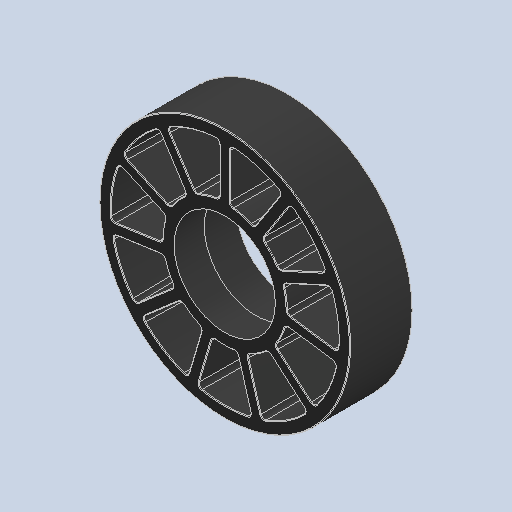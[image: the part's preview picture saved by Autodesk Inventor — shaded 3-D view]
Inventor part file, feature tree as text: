
AUTODESK INVENTOR PART (.ipt)
format: ipt  version: 2022.3 (Build 263350000, 350)  size: 1,065,984 bytes
history: native  units: in
note: dims shown in document units (in); Inventor stores cm internally (conversion verified against a paired STEP export)
features: fillet x1
ambient origin geometry x8: Origin, YZ Plane, XZ Plane, XY Plane, X Axis, Y Axis, Z Axis, Center Point
bodies: Solid1 (feature_tree)
feature tree (1):
  fillet  "Fillet2"  [1 undecoded]
note: 1 required parameter value undecoded (feature->parameter linkage not recoverable at this tier; creation-order binding heuristic only, values carry confidence <= 0.55)
